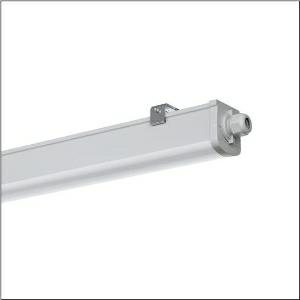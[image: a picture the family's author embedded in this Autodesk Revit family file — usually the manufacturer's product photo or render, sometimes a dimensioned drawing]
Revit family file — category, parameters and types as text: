
# Revit family: monsun_r__31_51fa207p430b_b845
name_source: partatom
category: Lighting Fixtures
units: mm (PartAtom-declared; Revit-internal decimal feet)

## family parameters
Cut with Voids When Loaded = No
Host = Face
Light Source = No
Part Type = Normal
Room Calculation Point = No
Round Connector Dimension = Use Diameter
Shared = No

## types (1)
- Monsun® 31 (1 x LED, 3800 lm, 28 W, 4000K)
    Apparent Load = 28 VA
    CIE Flux Codes = 42 72 91 92 100
    Color Rendering = 80
    Color Temperature = 4000K
    Default Elevation = 1800 mm
    Description = Monsun® 31, damp-proof luminaire, primary optical cover: diffuser, of PC, frosted, light emission: direct distribution, primary light characteristic: symmetric, installation type: surface-mounted, LED, rated luminous flux: 3.800lm, luminous efficacy: 136lm/W, light colour: 840, colour temperature: 4000K, control gear: ECG, with terminal, 3+1-pole, max. 2.5mm², through-wiring: 3x 2.5mm² + 1x 1.5mm², mains connection: 220..240V, AC, 50/60Hz, rated input power: 28W, housing, luminaire housing, of PC, light grey (RAL 7035), length: 1.458mm, width: 68mm, height: 76mm, protection rating (complete): IP66, insulation class (complete): insulation class II (safety insulation), certification: CE, ENEC, UKCA, protection symbol: D, impact resistance: IK08, permissible operating ambient temperature: -20..+40°C, corresponds to IFS (International Featured Standards) requirements for safety and quality in the food industry, packaging unit: 1 piece
    Height = 77 mm
    Lamp = 1 x LED
    Lamp Light Flux = 3800 lm
    Lamp Power = 28 W
    Lamp count = 1
    Length = 1518 mm
    Luminous efficacy = 136 lm/W
    Manufacturer = Siteco
    ModVariant = No
    Model = 51FA207P430B
    Mounting Place = Ceiling
    Mounting Type = Surface mounted
    Number of Poles = 1
    OnlyDefault = Yes
    Power Factor = 1
    Product Name = Monsun® 31
    Product group = damp-proof luminaire | ceiling mounted
    ProductGroupID = 300
    Protection Class = Protection class II
    Protection Degree = IP 66
    RLX_Detail_Level = 1
    RlxData = <blob elided: 33093 chars, md5=03f2df76>
    Socket = socket
    Standby Power = 0 W
    System Light Flux = 3800 lm
    System Power = 28 W
    Type Comments = Product without accessories
    Type Image = l_1006174.jpg
    URL = http://relux.com
    VarID = ---
    Voltage = 0 V
    Weight = 0.00 kg
    Width = 69 mm

## geometry (parser evidence)
native form markers: Blend x4, Sweep x12
no freeform markers — native parametric forms only
